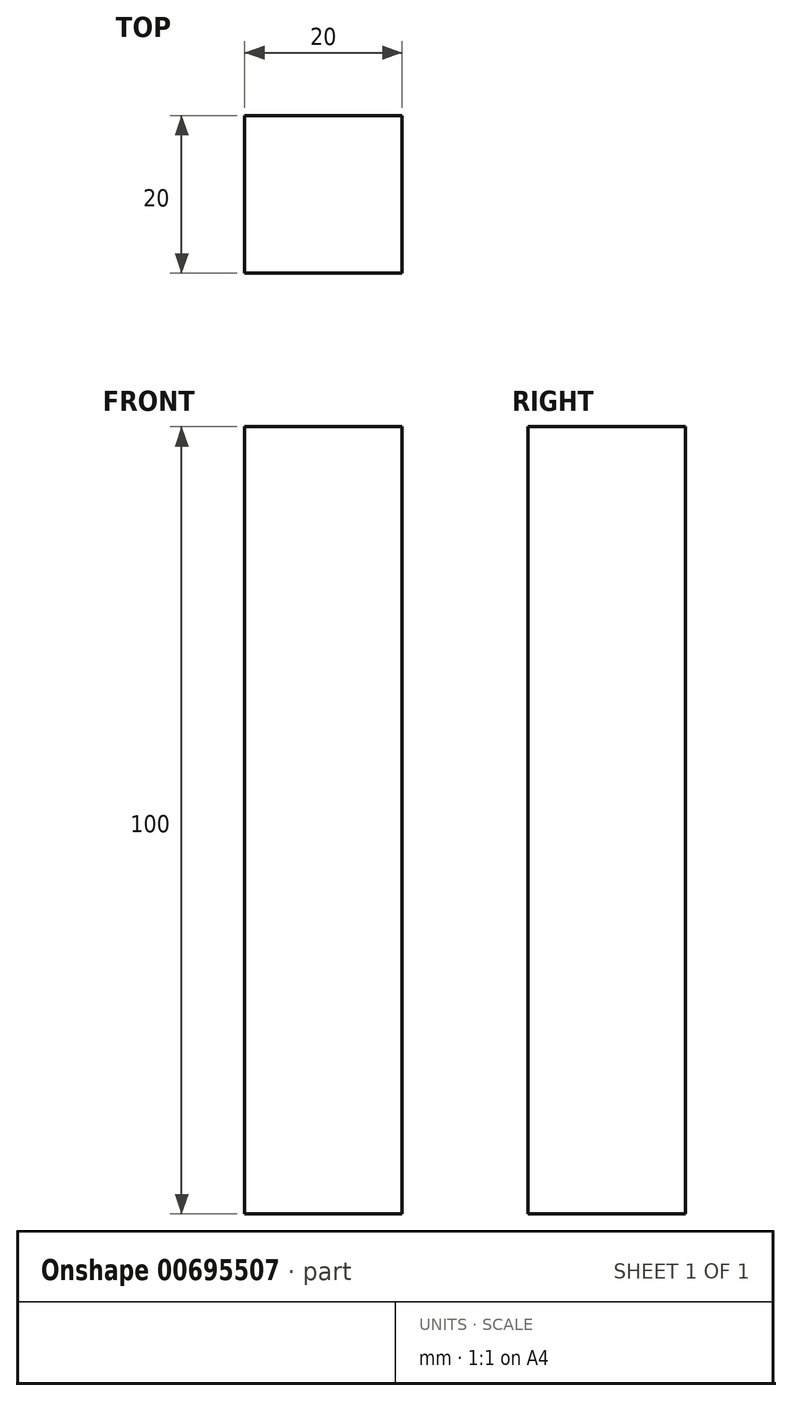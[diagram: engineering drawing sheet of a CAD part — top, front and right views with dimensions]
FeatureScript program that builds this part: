
annotation { "Feature Type Name" : "Feature", "Feature Type Description" : "" }
export const myFeature = defineFeature(function(context is Context, id is Id, definition is map)
    precondition{}
    {
        {
            var Q0;
            Q0=qCreatedBy(makeId("Top.planeOp"),FACE);
            var sketch = newSketch(context, id + "F0", { "sketchPlane" : qUnion([Q0])});
            skLineSegment(sketch, "E0.bottom", {"start": v(0, 0) * mm, "end": v(20, 0) * mm});
            skLineSegment(sketch, "E0.top", {"start": v(0, 20) * mm, "end": v(20, 20) * mm});
            skLineSegment(sketch, "E0.left", {"start": v(0, 0) * mm, "end": v(0, 20) * mm});
            skLineSegment(sketch, "E0.right", {"start": v(20, 0) * mm, "end": v(20, 20) * mm});
            skSolve(sketch);
        }
        {
            var Q0;
            Q0=makeQuery(id+"F0.imprint","IMPRINT",FACE,{"disambiguationData":[TD([[makeQuery(id+"F0.imprint","IMPRINT",EDGE,{"derivedFrom":sQuery(id+"F0.wireOp",EDGE,"E0.bottom")}),1.0]])]});
            extrude(context, id + "F1", {"entities" : qUnion([Q0]), "depth" : 100 * mm, "offsetDistance" : 25 * mm});
        }
    });
